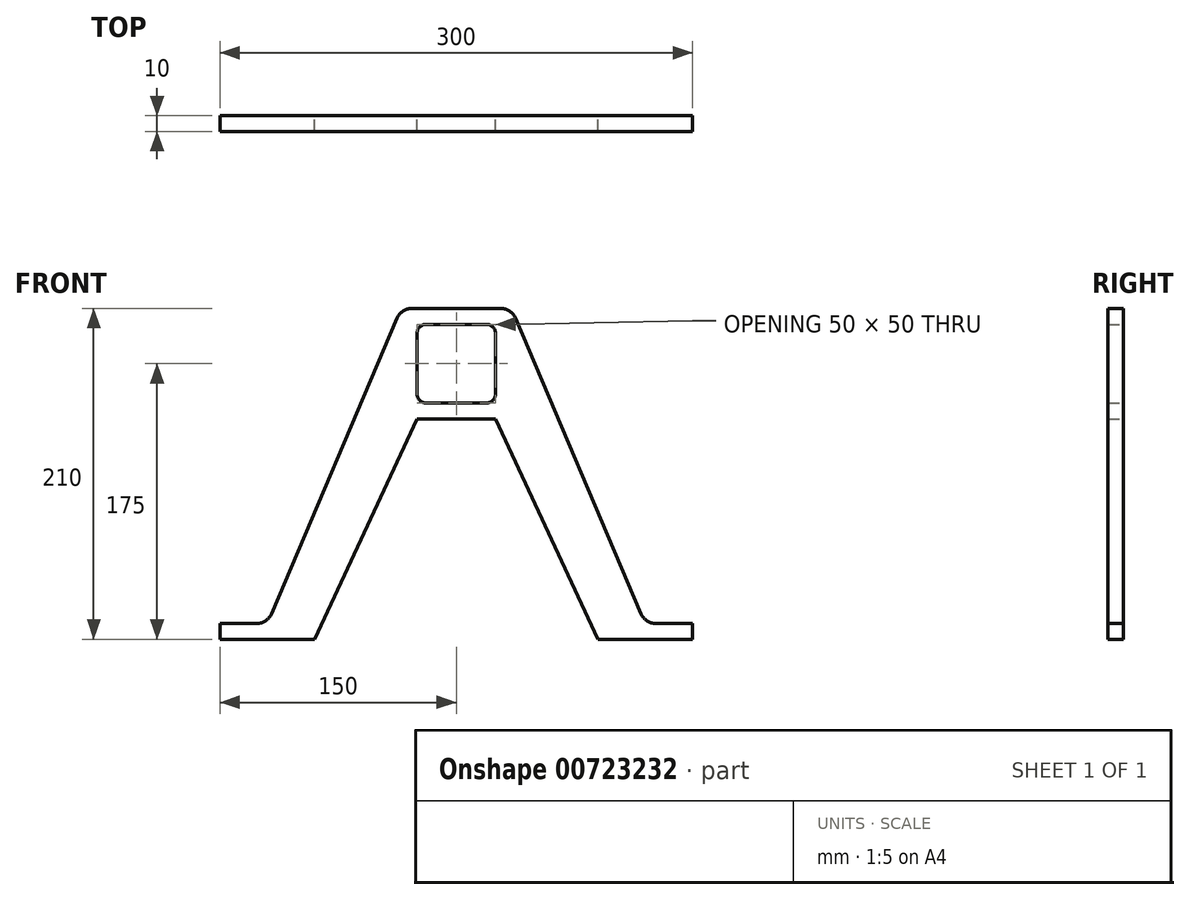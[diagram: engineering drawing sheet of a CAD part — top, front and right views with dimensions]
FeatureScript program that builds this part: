
annotation { "Feature Type Name" : "Feature", "Feature Type Description" : "" }
export const myFeature = defineFeature(function(context is Context, id is Id, definition is map)
    precondition{}
    {
        {
            var Q0;
            Q0=qCreatedBy(makeId("Front.planeOp"),FACE);
            var sketch = newSketch(context, id + "F0", { "sketchPlane" : qUnion([Q0])});
            skLineSegment(sketch, "E0.bottom", {"start": v(-19, 25) * mm, "end": v(19, 25) * mm});
            skLineSegment(sketch, "E0.top", {"start": v(-19, -25) * mm, "end": v(19, -25) * mm});
            skLineSegment(sketch, "E0.left", {"start": v(-25, 19) * mm, "end": v(-25, -19) * mm});
            skLineSegment(sketch, "E0.right", {"start": v(25, 19) * mm, "end": v(25, -19) * mm});
            skPoint(sketch, "E1.visualSharp", {"position": v(-25, 25) * mm});
            skArc(sketch, "E1.filletArc", {"start": v(-19, 25) * mm, "mid": v(-23.24, 23.24) * mm, "end": v(-25, 19) * mm});
            skPoint(sketch, "E2.visualSharp", {"position": v(-25, -25) * mm});
            skArc(sketch, "E2.filletArc", {"start": v(-25, -19) * mm, "mid": v(-23.24, -23.24) * mm, "end": v(-19, -25) * mm});
            skPoint(sketch, "E3.visualSharp", {"position": v(25, -25) * mm});
            skArc(sketch, "E3.filletArc", {"start": v(19, -25) * mm, "mid": v(23.24, -23.24) * mm, "end": v(25, -19) * mm});
            skPoint(sketch, "E4.visualSharp", {"position": v(25, 25) * mm});
            skArc(sketch, "E4.filletArc", {"start": v(25, 19) * mm, "mid": v(23.24, 23.24) * mm, "end": v(19, 25) * mm});
            skLineSegment(sketch, "E5", {"start": v(-150, -175) * mm, "end": v(-90, -175) * mm});
            skLineSegment(sketch, "E6", {"start": v(-150, -175) * mm, "end": v(-150, -165) * mm});
            skLineSegment(sketch, "E7", {"start": v(-150, -165) * mm, "end": v(-126.62, -165) * mm});
            skLineSegment(sketch, "E8", {"start": v(-117.41, -158.91) * mm, "end": v(-37.59, 28.91) * mm});
            skLineSegment(sketch, "E9", {"start": v(-28.38, 35) * mm, "end": v(28.38, 35) * mm});
            skLineSegment(sketch, "E10", {"start": v(37.59, 28.91) * mm, "end": v(117.41, -158.91) * mm});
            skLineSegment(sketch, "E11", {"start": v(126.62, -165) * mm, "end": v(150, -165) * mm});
            skLineSegment(sketch, "E12", {"start": v(150, -165) * mm, "end": v(150, -175) * mm});
            skPoint(sketch, "E13.visualSharp", {"position": v(-120, -165) * mm});
            skArc(sketch, "E13.filletArc", {"start": v(-126.62, -165) * mm, "mid": v(-121.1, -163.34) * mm, "end": v(-117.41, -158.91) * mm});
            skPoint(sketch, "E14.visualSharp", {"position": v(120, -165) * mm});
            skArc(sketch, "E14.filletArc", {"start": v(117.41, -158.91) * mm, "mid": v(121.1, -163.34) * mm, "end": v(126.62, -165) * mm});
            skPoint(sketch, "E15.visualSharp", {"position": v(-35, 35) * mm});
            skArc(sketch, "E15.filletArc", {"start": v(-28.38, 35) * mm, "mid": v(-33.9, 33.34) * mm, "end": v(-37.59, 28.91) * mm});
            skPoint(sketch, "E16.visualSharp", {"position": v(35, 35) * mm});
            skArc(sketch, "E16.filletArc", {"start": v(37.59, 28.91) * mm, "mid": v(33.9, 33.34) * mm, "end": v(28.38, 35) * mm});
            skLineSegment(sketch, "E17", {"start": v(-90, -175) * mm, "end": v(-25, -35) * mm});
            skLineSegment(sketch, "E18", {"start": v(-25, -35) * mm, "end": v(25, -35) * mm});
            skLineSegment(sketch, "E19", {"start": v(25, -35) * mm, "end": v(90, -175) * mm});
            skLineSegment(sketch, "E20.trimOffspring", {"start": v(90, -175) * mm, "end": v(150, -175) * mm});
            skSolve(sketch);
        }
        {
            var Q0;
            Q0=makeQuery(id+"F0.imprint","IMPRINT",FACE,{"disambiguationData":[TD([[makeQuery(id+"F0.imprint","IMPRINT",EDGE,{"derivedFrom":sQuery(id+"F0.wireOp",EDGE,"E0.bottom")}),1.0]])]});
            extrude(context, id + "F1", {"entities" : qUnion([Q0]), "endBound" : BoundingType.SYMMETRIC, "depth" : 10 * mm, "offsetDistance" : 25 * mm});
        }
    });
